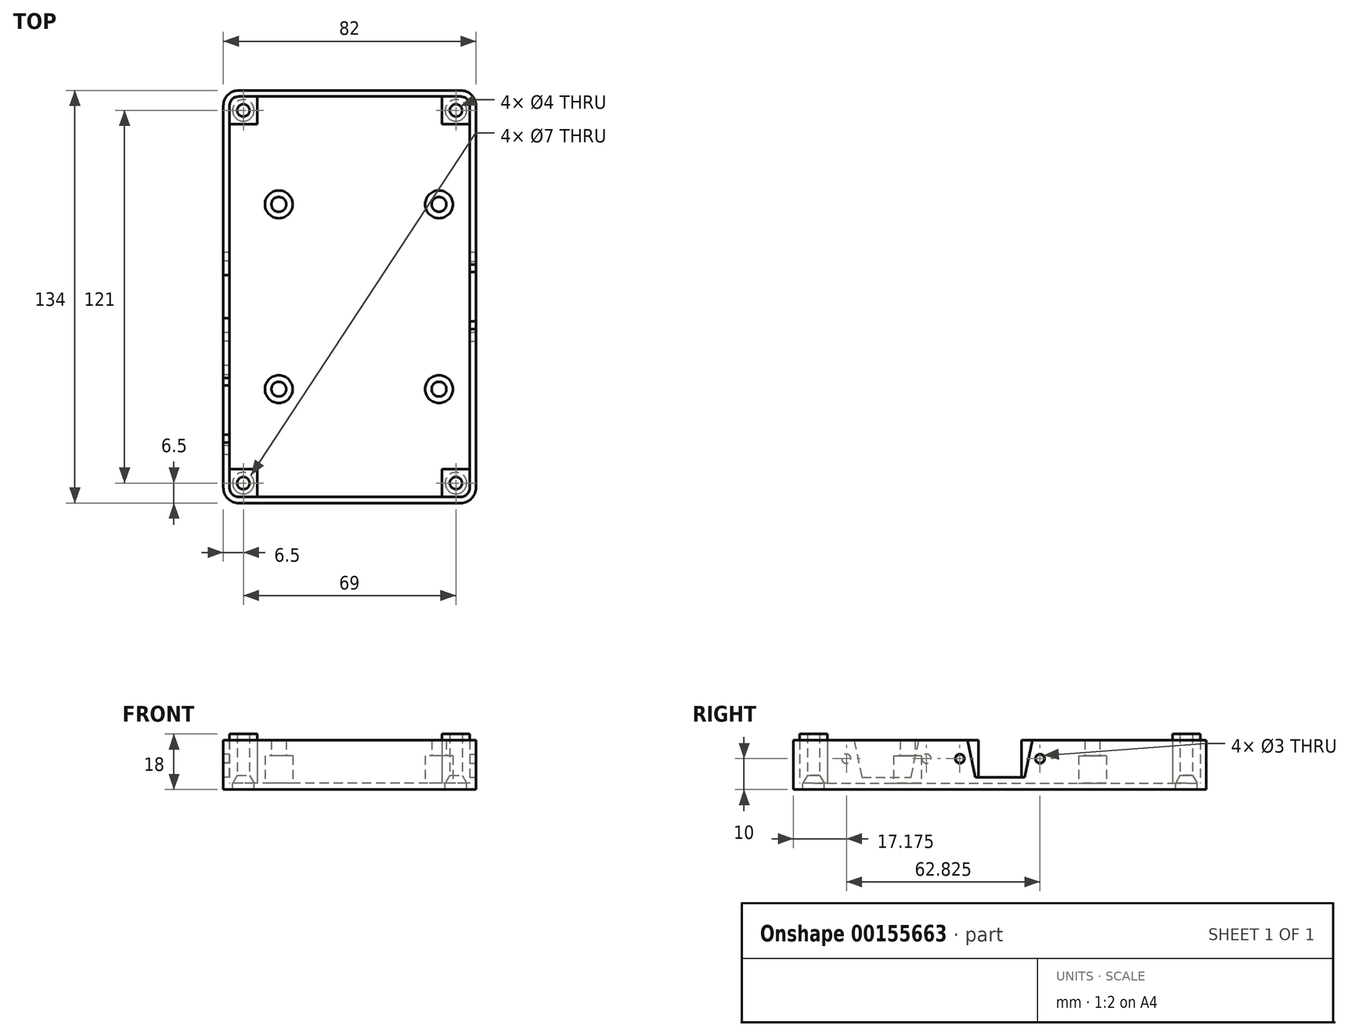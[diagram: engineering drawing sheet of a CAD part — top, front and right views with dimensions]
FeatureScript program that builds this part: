
annotation { "Feature Type Name" : "Feature", "Feature Type Description" : "" }
export const myFeature = defineFeature(function(context is Context, id is Id, definition is map)
    precondition{}
    {
        {
            var Q0;
            Q0=qCreatedBy(makeId("Top.planeOp"),FACE);
            var sketch = newSketch(context, id + "F0", { "sketchPlane" : qUnion([Q0])});
            skLineSegment(sketch, "E0.bottom", {"start": v(36, -67) * mm, "end": v(-36, -67) * mm});
            skLineSegment(sketch, "E0.top", {"start": v(36, 67) * mm, "end": v(-36, 67) * mm});
            skLineSegment(sketch, "E0.left", {"start": v(41, -62) * mm, "end": v(41, 62) * mm});
            skLineSegment(sketch, "E0.right", {"start": v(-41, -62) * mm, "end": v(-41, 62) * mm});
            skPoint(sketch, "E0.middle", {"position": v(0, 0) * mm});
            skPoint(sketch, "E1.visualSharp", {"position": v(-41, 67) * mm});
            skArc(sketch, "E1.filletArc", {"start": v(-36, 67) * mm, "mid": v(-39.54, 65.54) * mm, "end": v(-41, 62) * mm});
            skPoint(sketch, "E2.visualSharp", {"position": v(41, 67) * mm});
            skArc(sketch, "E2.filletArc", {"start": v(41, 62) * mm, "mid": v(39.54, 65.54) * mm, "end": v(36, 67) * mm});
            skPoint(sketch, "E3.visualSharp", {"position": v(41, -67) * mm});
            skArc(sketch, "E3.filletArc", {"start": v(36, -67) * mm, "mid": v(39.54, -65.54) * mm, "end": v(41, -62) * mm});
            skPoint(sketch, "E4.visualSharp", {"position": v(-41, -67) * mm});
            skArc(sketch, "E4.filletArc", {"start": v(-41, -62) * mm, "mid": v(-39.54, -65.54) * mm, "end": v(-36, -67) * mm});
            skSolve(sketch);
        }
        {
            var Q0;
            Q0 = qSketchRegion(id + "F0", true);
            extrude(context, id + "F1", {"entities" : qUnion([Q0]), "depth" : 16 * mm});
        }
        {
            var Q0;
            Q0=makeQuery(id+"F1.opExtrude","CAP_FACE",FACE,{"disambiguationData":[OSD([sQuery(id+"F0.wireOp",EDGE,"E0.bottom"),sQuery(id+"F0.wireOp",EDGE,"E0.top"),sQuery(id+"F0.wireOp",EDGE,"E0.left"),sQuery(id+"F0.wireOp",EDGE,"E0.right"),sQuery(id+"F0.wireOp",EDGE,"E1.filletArc"),sQuery(id+"F0.wireOp",EDGE,"E2.filletArc"),sQuery(id+"F0.wireOp",EDGE,"E3.filletArc"),sQuery(id+"F0.wireOp",EDGE,"E4.filletArc")])],"isStart":false});
            shell(context, id + "F2", {"entities" : qUnion([Q0]), "thickness" : 2 * mm});
        }
        {
            var Q0;
            Q0=makeQuery(id+"F2.opShell","OFFSET_FACE",FACE,{"disambiguationData":[OSD([sQuery(id+"F0.wireOp",EDGE,"E0.bottom"),sQuery(id+"F0.wireOp",EDGE,"E0.top"),sQuery(id+"F0.wireOp",EDGE,"E0.left"),sQuery(id+"F0.wireOp",EDGE,"E0.right"),sQuery(id+"F0.wireOp",EDGE,"E1.filletArc"),sQuery(id+"F0.wireOp",EDGE,"E2.filletArc"),sQuery(id+"F0.wireOp",EDGE,"E3.filletArc"),sQuery(id+"F0.wireOp",EDGE,"E4.filletArc")])]});
            var sketch = newSketch(context, id + "F3", { "sketchPlane" : qUnion([Q0])});
            skCircle(sketch, "E5", {"center": v(-23, 30) * mm, "radius": 4.5 * mm});
            skCircle(sketch, "E6", {"center": v(29, 30) * mm, "radius": 4.5 * mm});
            skCircle(sketch, "E7", {"center": v(-23, -30) * mm, "radius": 4.5 * mm});
            skCircle(sketch, "E8", {"center": v(29, -30) * mm, "radius": 4.5 * mm});
            skLineSegment(sketch, "E9.bottom", {"start": v(-30, 56) * mm, "end": v(-39, 56) * mm});
            skLineSegment(sketch, "E9.top", {"start": v(-30, 65) * mm, "end": v(-39, 65) * mm});
            skLineSegment(sketch, "E9.left", {"start": v(-30, 56) * mm, "end": v(-30, 65) * mm});
            skLineSegment(sketch, "E9.right", {"start": v(-39, 56) * mm, "end": v(-39, 65) * mm});
            skPoint(sketch, "E9.middle", {"position": v(-34.5, 60.5) * mm});
            skLineSegment(sketch, "E10.bottom", {"start": v(39, 56) * mm, "end": v(30, 56) * mm});
            skLineSegment(sketch, "E10.top", {"start": v(39, 65) * mm, "end": v(30, 65) * mm});
            skLineSegment(sketch, "E10.left", {"start": v(39, 56) * mm, "end": v(39, 65) * mm});
            skLineSegment(sketch, "E10.right", {"start": v(30, 56) * mm, "end": v(30, 65) * mm});
            skPoint(sketch, "E10.middle", {"position": v(34.5, 60.5) * mm});
            skPoint(sketch, "E11.MirrorP", {"position": v(-34.5, -60.5) * mm});
            skLineSegment(sketch, "E12.MirrorCS", {"start": v(-30, -65) * mm, "end": v(-39, -65) * mm});
            skLineSegment(sketch, "E13.MirrorCS", {"start": v(30, -56) * mm, "end": v(30, -65) * mm});
            skLineSegment(sketch, "E14.MirrorCS", {"start": v(39, -56) * mm, "end": v(39, -65) * mm});
            skPoint(sketch, "E15.MirrorP", {"position": v(34.5, -60.5) * mm});
            skLineSegment(sketch, "E16.MirrorCS", {"start": v(-30, -56) * mm, "end": v(-39, -56) * mm});
            skLineSegment(sketch, "E17.MirrorCS", {"start": v(-30, -56) * mm, "end": v(-30, -65) * mm});
            skLineSegment(sketch, "E18.MirrorCS", {"start": v(-39, -56) * mm, "end": v(-39, -65) * mm});
            skLineSegment(sketch, "E19.MirrorCS", {"start": v(39, -65) * mm, "end": v(30, -65) * mm});
            skLineSegment(sketch, "E20.MirrorCS", {"start": v(39, -56) * mm, "end": v(30, -56) * mm});
            skLineSegment(sketch, "E21.bottom", {"start": v(-39, 56) * mm, "end": v(-37, 56) * mm});
            skLineSegment(sketch, "E21.top", {"start": v(-39, -56) * mm, "end": v(-37, -56) * mm});
            skLineSegment(sketch, "E21.left", {"start": v(-39, 56) * mm, "end": v(-39, -56) * mm});
            skLineSegment(sketch, "E21.right", {"start": v(-37, 56) * mm, "end": v(-37, -56) * mm});
            skLineSegment(sketch, "E22.bottom", {"start": v(39, -56) * mm, "end": v(37, -56) * mm});
            skLineSegment(sketch, "E22.top", {"start": v(39, 56) * mm, "end": v(37, 56) * mm});
            skLineSegment(sketch, "E22.left", {"start": v(39, -56) * mm, "end": v(39, 56) * mm});
            skLineSegment(sketch, "E22.right", {"start": v(37, -56) * mm, "end": v(37, 56) * mm});
            skSolve(sketch);
        }
        {
            var Q0;
            Q0=makeQuery(id+"F3.imprint","IMPRINT",FACE,{"disambiguationData":[TD([[makeQuery(id+"F3.imprint","IMPRINT",EDGE,{"derivedFrom":sQuery(id+"F3.wireOp",EDGE,"E5")}),1.0]])]});
            var Q1;
            Q1=makeQuery(id+"F3.imprint","IMPRINT",FACE,{"disambiguationData":[TD([[makeQuery(id+"F3.imprint","IMPRINT",EDGE,{"derivedFrom":sQuery(id+"F3.wireOp",EDGE,"E7")}),1.0]])]});
            var Q2;
            Q2=makeQuery(id+"F3.imprint","IMPRINT",FACE,{"disambiguationData":[TD([[makeQuery(id+"F3.imprint","IMPRINT",EDGE,{"derivedFrom":sQuery(id+"F3.wireOp",EDGE,"E8")}),1.0]])]});
            var Q3;
            Q3=makeQuery(id+"F3.imprint","IMPRINT",FACE,{"disambiguationData":[TD([[makeQuery(id+"F3.imprint","IMPRINT",EDGE,{"derivedFrom":sQuery(id+"F3.wireOp",EDGE,"E6")}),1.0]])]});
            extrude(context, id + "F4", {"entities" : qUnion([Q0, Q1, Q2, Q3]), "operationType" : NewBodyOperationType.ADD, "depth" : 9 * mm});
        }
        {
            var Q0;
            Q0=makeQuery(id+"F4.opExtrude","CAP_FACE",FACE,{"disambiguationData":[OSD([sQuery(id+"F3.wireOp",EDGE,"E5")])],"isStart":false});
            var Q1;
            Q1=makeQuery(id+"F4.opExtrude","CAP_FACE",FACE,{"disambiguationData":[OSD([sQuery(id+"F3.wireOp",EDGE,"E6")])],"isStart":false});
            cPlane(context, id + "F5", {"entities" : qUnion([Q0, Q1]), "cplaneType" : CPlaneType.MID_PLANE, "offset" : 25 * mm, "width" : 150 * mm, "height" : 150 * mm});
        }
        {
            var Q0;
            Q0=qCreatedBy(id+"F5.planeOp",FACE);
            var sketch = newSketch(context, id + "F6", { "sketchPlane" : qUnion([Q0])});
            skCircle(sketch, "E23", {"center": v(-23, 30) * mm, "radius": 2.4 * mm});
            skCircle(sketch, "E24", {"center": v(29, 30) * mm, "radius": 2.4 * mm});
            skCircle(sketch, "E25", {"center": v(-23, -30) * mm, "radius": 2.4 * mm});
            skCircle(sketch, "E26", {"center": v(29, -30) * mm, "radius": 2.4 * mm});
            skSolve(sketch);
        }
        {
            var Q0;
            Q0 = qSketchRegion(id + "F6", true);
            extrude(context, id + "F7", {"entities" : qUnion([Q0]), "operationType" : NewBodyOperationType.ADD, "depth" : 5 * mm});
        }
        {
            var Q0;
            {var subQ4=sQuery(id+"F3.wireOp",EDGE,"E9.bottom");Q0=makeQuery(id+"F3.imprint","IMPRINT",FACE,{"disambiguationData":[TD([[makeQuery(id+"F3.imprint","IMPRINT",EDGE,{"derivedFrom":subQ4}),-1.0]])]});}
            var Q1;
            {var subQ4=sQuery(id+"F3.wireOp",EDGE,"E10.bottom");Q1=makeQuery(id+"F3.imprint","IMPRINT",FACE,{"disambiguationData":[TD([[makeQuery(id+"F3.imprint","IMPRINT",EDGE,{"derivedFrom":subQ4}),-1.0]])]});}
            var Q2;
            {var subQ3=sQuery(id+"F3.wireOp",EDGE,"E13.MirrorCS");Q2=makeQuery(id+"F3.imprint","IMPRINT",FACE,{"disambiguationData":[TD([[makeQuery(id+"F3.imprint","IMPRINT",EDGE,{"derivedFrom":subQ3}),1.0]])]});}
            var Q3;
            {var subQ3=sQuery(id+"F3.wireOp",EDGE,"E16.MirrorCS");Q3=makeQuery(id+"F3.imprint","IMPRINT",FACE,{"disambiguationData":[TD([[makeQuery(id+"F3.imprint","IMPRINT",EDGE,{"derivedFrom":subQ3}),1.0]])]});}
            var Q4;
            Q4=makeQuery(id+"F3.imprint","IMPRINT",FACE,{"disambiguationData":[TD([[makeQuery(id+"F3.imprint","IMPRINT",EDGE,{"derivedFrom":sQuery(id+"F3.wireOp",EDGE,"E21.bottom")}),-1.0]])]});
            var Q5;
            Q5=makeQuery(id+"F3.imprint","IMPRINT",FACE,{"disambiguationData":[TD([[makeQuery(id+"F3.imprint","IMPRINT",EDGE,{"derivedFrom":sQuery(id+"F3.wireOp",EDGE,"E22.bottom")}),-1.0]])]});
            extrude(context, id + "F8", {"entities" : qUnion([Q0, Q1, Q2, Q3, Q4, Q5]), "operationType" : NewBodyOperationType.ADD, "depth" : 16 * mm});
        }
        {
            var Q0;
            Q0=makeQuery(id+"F1.opExtrude","SWEPT_FACE",FACE,{"disambiguationData":[OSD([sQuery(id+"F0.wireOp",EDGE,"E0.right")])]});
            var sketch = newSketch(context, id + "F9", { "sketchPlane" : qUnion([Q0])});
            skCircle(sketch, "E27", {"center": v(-13, 10) * mm, "radius": 1.4 * mm});
            skCircle(sketch, "E28", {"center": v(13, 10) * mm, "radius": 1.4 * mm});
            skLineSegment(sketch, "E29.bottom", {"start": v(7, 4) * mm, "end": v(-7, 4) * mm});
            skLineSegment(sketch, "E29.top", {"start": v(7, 16) * mm, "end": v(-7, 16) * mm});
            skLineSegment(sketch, "E29.left", {"start": v(7, 4) * mm, "end": v(7, 16) * mm});
            skLineSegment(sketch, "E29.right", {"start": v(-7, 4) * mm, "end": v(-7, 16) * mm});
            skPoint(sketch, "E29.middle", {"position": v(0, 10) * mm});
            skCircle(sketch, "E30", {"center": v(23.83, 10) * mm, "radius": 1.5 * mm});
            skCircle(sketch, "E31", {"center": v(49.83, 10) * mm, "radius": 1.5 * mm});
            skLineSegment(sketch, "E32", {"start": v(26.33, 16) * mm, "end": v(47.33, 16) * mm});
            skLineSegment(sketch, "E33", {"start": v(47.33, 16) * mm, "end": v(44.83, 4) * mm});
            skLineSegment(sketch, "E34", {"start": v(44.83, 4) * mm, "end": v(28.83, 4) * mm});
            skLineSegment(sketch, "E35", {"start": v(28.83, 4) * mm, "end": v(26.33, 16) * mm});
            skLineSegment(sketch, "E36.bottom", {"start": v(-7, 16) * mm, "end": v(7, 16) * mm});
            skLineSegment(sketch, "E36.top", {"start": v(-7, 18) * mm, "end": v(7, 18) * mm});
            skLineSegment(sketch, "E36.left", {"start": v(-7, 16) * mm, "end": v(-7, 18) * mm});
            skLineSegment(sketch, "E36.right", {"start": v(7, 16) * mm, "end": v(7, 18) * mm});
            skLineSegment(sketch, "E37.top", {"start": v(26.33, 18) * mm, "end": v(47.33, 18) * mm});
            skLineSegment(sketch, "E37.left", {"start": v(26.33, 16) * mm, "end": v(26.33, 18) * mm});
            skLineSegment(sketch, "E37.right", {"start": v(47.33, 16) * mm, "end": v(47.33, 18) * mm});
            skSolve(sketch);
        }
        {
            var Q0;
            Q0=makeQuery(id+"F1.opExtrude","SWEPT_FACE",FACE,{"disambiguationData":[OSD([sQuery(id+"F0.wireOp",EDGE,"E0.left")])]});
            var sketch = newSketch(context, id + "F10", { "sketchPlane" : qUnion([Q0])});
            skCircle(sketch, "E38", {"center": v(-13, 10) * mm, "radius": 1.5 * mm});
            skCircle(sketch, "E39", {"center": v(13, 10) * mm, "radius": 1.5 * mm});
            skLineSegment(sketch, "E40", {"start": v(-10.5, 16) * mm, "end": v(10.5, 16) * mm});
            skLineSegment(sketch, "E41", {"start": v(10.5, 16) * mm, "end": v(8, 4) * mm});
            skLineSegment(sketch, "E42", {"start": v(8, 4) * mm, "end": v(-8, 4) * mm});
            skLineSegment(sketch, "E43", {"start": v(-8, 4) * mm, "end": v(-10.5, 16) * mm});
            skLineSegment(sketch, "E44.top", {"start": v(-10.5, 18) * mm, "end": v(10.5, 18) * mm});
            skLineSegment(sketch, "E44.left", {"start": v(-10.5, 16) * mm, "end": v(-10.5, 18) * mm});
            skLineSegment(sketch, "E44.right", {"start": v(10.5, 16) * mm, "end": v(10.5, 18) * mm});
            skSolve(sketch);
        }
        {
            var Q0;
            Q0 = qSketchRegion(id + "F9", true);
            extrude(context, id + "F11", {"entities" : qUnion([Q0]), "operationType" : NewBodyOperationType.REMOVE, "oppositeDirection" : true, "depth" : 4 * mm});
        }
        {
            var Q0;
            Q0 = qSketchRegion(id + "F10", true);
            extrude(context, id + "F12", {"entities" : qUnion([Q0]), "operationType" : NewBodyOperationType.REMOVE, "oppositeDirection" : true, "depth" : 4 * mm});
        }
        {
            var Q0;
            Q0=sQuery(id+"F3.wireOp",VERTEX,"E10.middle");
            var Q1;
            Q1=sQuery(id+"F3.wireOp",VERTEX,"E9.middle");
            var Q2;
            Q2=sQuery(id+"F3.wireOp",VERTEX,"E11.MirrorP");
            var Q3;
            Q3=sQuery(id+"F3.wireOp",VERTEX,"E15.MirrorP");
            var Q4;
            Q4=makeQuery(id+"F1.opExtrude","SWEPT_BODY",BODY,{"disambiguationData":[OSD([sQuery(id+"F0.wireOp",EDGE,"E0.bottom"),sQuery(id+"F0.wireOp",EDGE,"E0.top"),sQuery(id+"F0.wireOp",EDGE,"E0.left"),sQuery(id+"F0.wireOp",EDGE,"E0.right"),sQuery(id+"F0.wireOp",EDGE,"E1.filletArc"),sQuery(id+"F0.wireOp",EDGE,"E2.filletArc"),sQuery(id+"F0.wireOp",EDGE,"E3.filletArc"),sQuery(id+"F0.wireOp",EDGE,"E4.filletArc")])]});
            hole(context, id + "F13", {"style" : HoleStyle.C_SINK, "endStyle" : HoleEndStyle.THROUGH, "oppositeDirection" : true, "holeDiameter" : 4 * mm, "cSinkDiameter" : 7 * mm, "cSinkAngle" : 60 * degree, "locations" : qUnion([Q0, Q1, Q2, Q3]), "scope" : qUnion([Q4]), "isTappedThrough" : true});
        }
        {
            var Q0;
            Q0=sQuery(id+"F3.wireOp",VERTEX,"E9.middle");
            var Q1;
            Q1=sQuery(id+"F3.wireOp",VERTEX,"E11.MirrorP");
            var Q2;
            Q2=sQuery(id+"F3.wireOp",VERTEX,"E10.middle");
            var Q3;
            Q3=sQuery(id+"F3.wireOp",VERTEX,"E15.MirrorP");
            var Q4;
            Q4=makeQuery(id+"F1.opExtrude","SWEPT_BODY",BODY,{"disambiguationData":[OSD([sQuery(id+"F0.wireOp",EDGE,"E0.bottom"),sQuery(id+"F0.wireOp",EDGE,"E0.top"),sQuery(id+"F0.wireOp",EDGE,"E0.left"),sQuery(id+"F0.wireOp",EDGE,"E0.right"),sQuery(id+"F0.wireOp",EDGE,"E1.filletArc"),sQuery(id+"F0.wireOp",EDGE,"E2.filletArc"),sQuery(id+"F0.wireOp",EDGE,"E3.filletArc"),sQuery(id+"F0.wireOp",EDGE,"E4.filletArc")])]});
            hole(context, id + "F14", {"style" : HoleStyle.SIMPLE, "endStyle" : HoleEndStyle.THROUGH, "holeDiameter" : 7 * mm, "locations" : qUnion([Q0, Q1, Q2, Q3]), "scope" : qUnion([Q4]), "isTappedThrough" : true});
        }
    });
